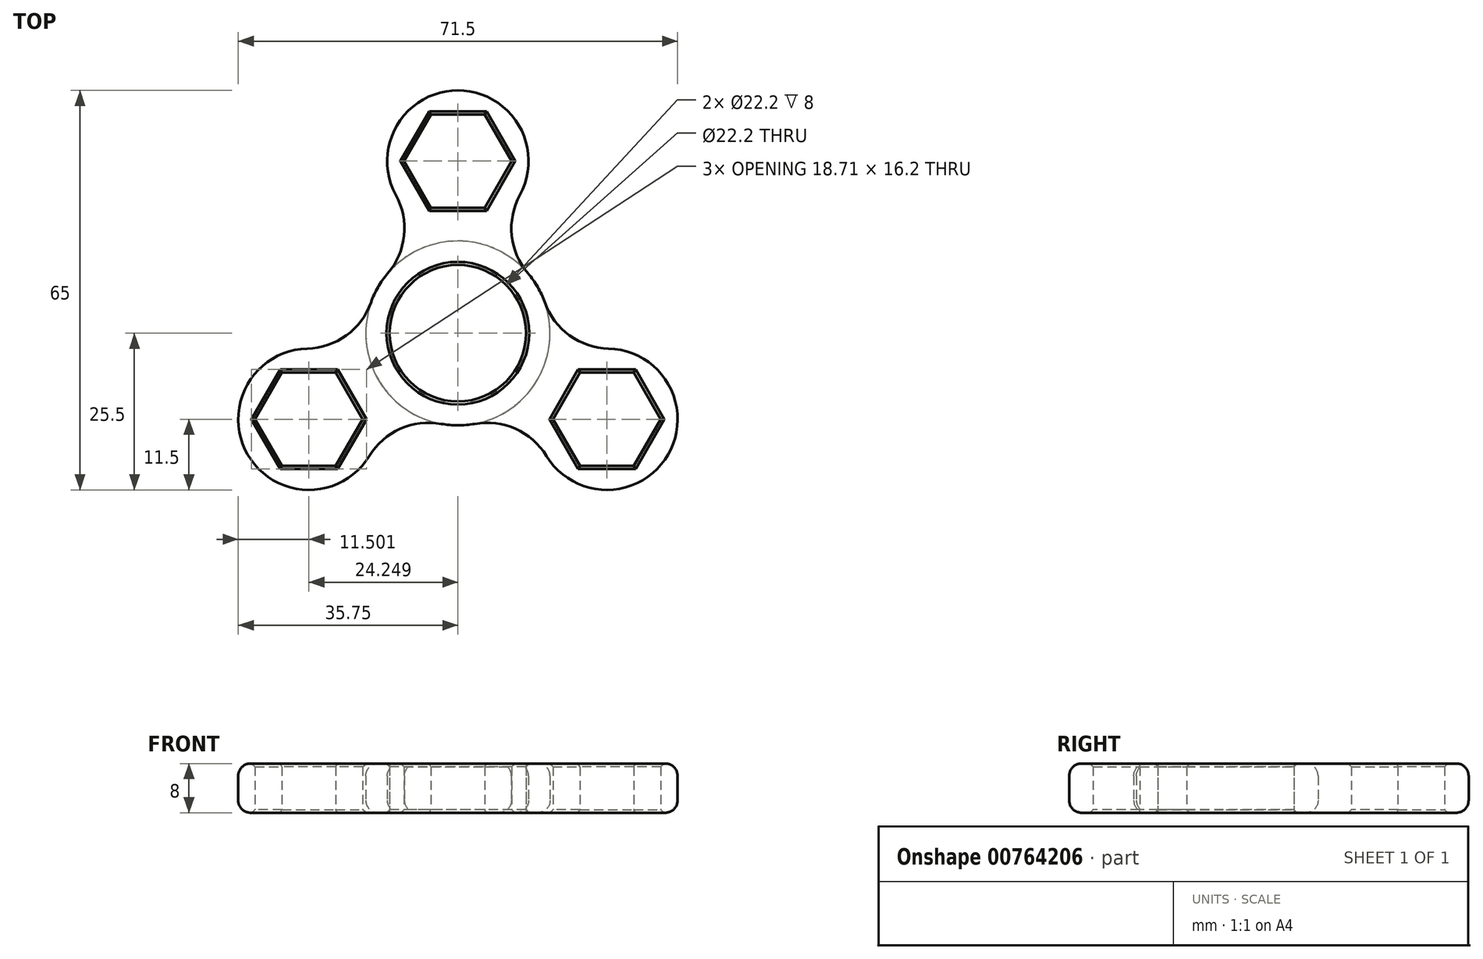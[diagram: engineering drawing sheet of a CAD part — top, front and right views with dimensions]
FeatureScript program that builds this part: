
annotation { "Feature Type Name" : "Feature", "Feature Type Description" : "" }
export const myFeature = defineFeature(function(context is Context, id is Id, definition is map)
    precondition{}
    {
        {
            var Q0;
            Q0=qCreatedBy(makeId("Top.planeOp"),FACE);
            var sketch = newSketch(context, id + "F0", { "sketchPlane" : qUnion([Q0])});
            skCircle(sketch, "E0", {"center": v(0, 0) * mm, "radius": 11.1 * mm});
            skArc(sketch, "E1", {"start": v(10.1, 22.48) * mm, "mid": v(0, 39.5) * mm, "end": v(-10.1, 22.48) * mm});
            skArc(sketch, "E2", {"start": v(-11.4, 9.74) * mm, "mid": v(0, -15) * mm, "end": v(11.4, 9.74) * mm});
            skArc(sketch, "E3", {"start": v(10.1, 22.48) * mm, "mid": v(8.77, 15.9) * mm, "end": v(11.4, 9.74) * mm});
            skLineSegment(sketch, "E4", {"start": v(0, -19.89) * mm, "end": v(0, 62.9) * mm, "construction": true});
            skArc(sketch, "E5.MirrorCS", {"start": v(-10.1, 22.48) * mm, "mid": v(-8.77, 15.9) * mm, "end": v(-11.4, 9.74) * mm});
            skCircle(sketch, "E6.cCircle", {"center": v(0, 28) * mm, "radius": 7.6 * mm, "construction": true});
            skLineSegment(sketch, "E6.0", {"start": v(4.39, 20.4) * mm, "end": v(-4.39, 20.4) * mm});
            skLineSegment(sketch, "E6.1", {"start": v(-4.39, 20.4) * mm, "end": v(-8.78, 28) * mm});
            skLineSegment(sketch, "E6.2", {"start": v(-8.78, 28) * mm, "end": v(-4.39, 35.6) * mm});
            skLineSegment(sketch, "E6.3", {"start": v(-4.39, 35.6) * mm, "end": v(4.39, 35.6) * mm});
            skLineSegment(sketch, "E6.4", {"start": v(4.39, 35.6) * mm, "end": v(8.78, 28) * mm});
            skLineSegment(sketch, "E6.5", {"start": v(8.78, 28) * mm, "end": v(4.39, 20.4) * mm});
            skPoint(sketch, "E6.0.midPoint", {"position": v(0, 20.4) * mm});
            skSolve(sketch);
        }
        {
            var Q0;
            Q0=makeQuery(id+"F0.imprint","IMPRINT",FACE,{"disambiguationData":[TD([[makeQuery(id+"F0.imprint","IMPRINT",EDGE,{"derivedFrom":sQuery(id+"F0.wireOp",EDGE,"E0")}),-1.0]])]});
            extrude(context, id + "F1", {"entities" : qUnion([Q0]), "depth" : 8 * mm, "offsetDistance" : 25 * mm});
        }
        {
            var Q0;
            Q0=makeQuery(id+"F1.opExtrude","SWEPT_BODY",BODY,{"disambiguationData":[OSD([sQuery(id+"F0.wireOp",EDGE,"E0"),sQuery(id+"F0.wireOp",EDGE,"PvTHQTtv-MwDr-1RPm-Ui1H-ZR7QVBU8jPbe"),sQuery(id+"F0.wireOp",EDGE,"E1"),sQuery(id+"F0.wireOp",EDGE,"E2"),sQuery(id+"F0.wireOp",EDGE,"E3"),sQuery(id+"F0.wireOp",EDGE,"E5.MirrorCS")])]});
            var Q1;
            Q1=makeQuery(id+"F1.opExtrude","CAP_EDGE",EDGE,{"disambiguationData":[OSD([sQuery(id+"F0.wireOp",EDGE,"E0")])],"isStart":false});
            circularPattern(context, id + "F2", {"entities" : qUnion([Q0]), "axis" : qUnion([Q1]), "angle" : 360 * degree, "instanceCount" : 3, "equalSpace" : true});
        }
        {
            var Q0;
            Q0=makeQuery(id+"F2.opPattern","COPY",EDGE,{"derivedFrom":makeQuery(id+"F1.opExtrude","CAP_EDGE",EDGE,{"disambiguationData":[OSD([sQuery(id+"F0.wireOp",EDGE,"E3")])],"isStart":false}),"instanceName":"2"});
            fillet(context, id + "F3", {"entities" : qUnion([Q0]), "radius" : 2 * mm, "tangentPropagation" : true, "allowEdgeOverflow" : false});
        }
        {
            var Q0;
            Q0=makeQuery(id+"F2.opPattern","COPY",EDGE,{"derivedFrom":makeQuery(id+"F1.opExtrude","CAP_EDGE",EDGE,{"disambiguationData":[OSD([sQuery(id+"F0.wireOp",EDGE,"E1")])],"isStart":false}),"instanceName":"1"});
            var Q1;
            Q1=makeQuery(id+"F1.opExtrude","CAP_EDGE",EDGE,{"disambiguationData":[OSD([sQuery(id+"F0.wireOp",EDGE,"E5.MirrorCS")])],"isStart":false});
            var Q2;
            Q2=makeQuery(id+"F2.opPattern","COPY",EDGE,{"derivedFrom":makeQuery(id+"F1.opExtrude","CAP_EDGE",EDGE,{"disambiguationData":[OSD([sQuery(id+"F0.wireOp",EDGE,"E1")])],"isStart":true}),"instanceName":"1"});
            var Q3;
            Q3=makeQuery(id+"F2.opPattern","COPY",EDGE,{"derivedFrom":makeQuery(id+"F1.opExtrude","CAP_EDGE",EDGE,{"disambiguationData":[OSD([sQuery(id+"F0.wireOp",EDGE,"E1")])],"isStart":true}),"instanceName":"2"});
            var Q4;
            Q4=makeQuery(id+"F1.opExtrude","CAP_EDGE",EDGE,{"disambiguationData":[OSD([sQuery(id+"F0.wireOp",EDGE,"E5.MirrorCS")])],"isStart":true});
            fillet(context, id + "F4", {"entities" : qUnion([Q0, Q1, Q2, Q3, Q4]), "radius" : 2 * mm, "tangentPropagation" : true, "allowEdgeOverflow" : false});
        }
        {
            var Q0;
            Q0=makeQuery(id+"F1.opExtrude","CAP_EDGE",EDGE,{"disambiguationData":[OSD([sQuery(id+"F0.wireOp",EDGE,"E6.0")])],"isStart":false});
            var Q1;
            Q1=makeQuery(id+"F1.opExtrude","CAP_EDGE",EDGE,{"disambiguationData":[OSD([sQuery(id+"F0.wireOp",EDGE,"E6.1")])],"isStart":false});
            var Q2;
            Q2=makeQuery(id+"F1.opExtrude","CAP_EDGE",EDGE,{"disambiguationData":[OSD([sQuery(id+"F0.wireOp",EDGE,"E6.5")])],"isStart":false});
            var Q3;
            Q3=makeQuery(id+"F1.opExtrude","CAP_EDGE",EDGE,{"disambiguationData":[OSD([sQuery(id+"F0.wireOp",EDGE,"E6.4")])],"isStart":false});
            var Q4;
            Q4=makeQuery(id+"F1.opExtrude","CAP_EDGE",EDGE,{"disambiguationData":[OSD([sQuery(id+"F0.wireOp",EDGE,"E6.3")])],"isStart":false});
            var Q5;
            Q5=makeQuery(id+"F1.opExtrude","CAP_EDGE",EDGE,{"disambiguationData":[OSD([sQuery(id+"F0.wireOp",EDGE,"E6.2")])],"isStart":false});
            var Q6;
            Q6=makeQuery(id+"F2.opPattern","COPY",EDGE,{"derivedFrom":makeQuery(id+"F1.opExtrude","CAP_EDGE",EDGE,{"disambiguationData":[OSD([sQuery(id+"F0.wireOp",EDGE,"E6.5")])],"isStart":false}),"instanceName":"1"});
            var Q7;
            Q7=makeQuery(id+"F2.opPattern","COPY",EDGE,{"derivedFrom":makeQuery(id+"F1.opExtrude","CAP_EDGE",EDGE,{"disambiguationData":[OSD([sQuery(id+"F0.wireOp",EDGE,"E6.0")])],"isStart":false}),"instanceName":"1"});
            var Q8;
            Q8=makeQuery(id+"F2.opPattern","COPY",EDGE,{"derivedFrom":makeQuery(id+"F1.opExtrude","CAP_EDGE",EDGE,{"disambiguationData":[OSD([sQuery(id+"F0.wireOp",EDGE,"E6.1")])],"isStart":false}),"instanceName":"1"});
            var Q9;
            Q9=makeQuery(id+"F2.opPattern","COPY",EDGE,{"derivedFrom":makeQuery(id+"F1.opExtrude","CAP_EDGE",EDGE,{"disambiguationData":[OSD([sQuery(id+"F0.wireOp",EDGE,"E6.2")])],"isStart":false}),"instanceName":"1"});
            var Q10;
            Q10=makeQuery(id+"F2.opPattern","COPY",EDGE,{"derivedFrom":makeQuery(id+"F1.opExtrude","CAP_EDGE",EDGE,{"disambiguationData":[OSD([sQuery(id+"F0.wireOp",EDGE,"E6.3")])],"isStart":false}),"instanceName":"1"});
            var Q11;
            Q11=makeQuery(id+"F2.opPattern","COPY",EDGE,{"derivedFrom":makeQuery(id+"F1.opExtrude","CAP_EDGE",EDGE,{"disambiguationData":[OSD([sQuery(id+"F0.wireOp",EDGE,"E6.4")])],"isStart":false}),"instanceName":"1"});
            var Q12;
            Q12=makeQuery(id+"F2.opPattern","COPY",EDGE,{"derivedFrom":makeQuery(id+"F1.opExtrude","CAP_EDGE",EDGE,{"disambiguationData":[OSD([sQuery(id+"F0.wireOp",EDGE,"E6.0")])],"isStart":false}),"instanceName":"2"});
            var Q13;
            Q13=makeQuery(id+"F2.opPattern","COPY",EDGE,{"derivedFrom":makeQuery(id+"F1.opExtrude","CAP_EDGE",EDGE,{"disambiguationData":[OSD([sQuery(id+"F0.wireOp",EDGE,"E6.1")])],"isStart":false}),"instanceName":"2"});
            var Q14;
            Q14=makeQuery(id+"F2.opPattern","COPY",EDGE,{"derivedFrom":makeQuery(id+"F1.opExtrude","CAP_EDGE",EDGE,{"disambiguationData":[OSD([sQuery(id+"F0.wireOp",EDGE,"E6.2")])],"isStart":false}),"instanceName":"2"});
            var Q15;
            Q15=makeQuery(id+"F2.opPattern","COPY",EDGE,{"derivedFrom":makeQuery(id+"F1.opExtrude","CAP_EDGE",EDGE,{"disambiguationData":[OSD([sQuery(id+"F0.wireOp",EDGE,"E6.3")])],"isStart":false}),"instanceName":"2"});
            var Q16;
            Q16=makeQuery(id+"F2.opPattern","COPY",EDGE,{"derivedFrom":makeQuery(id+"F1.opExtrude","CAP_EDGE",EDGE,{"disambiguationData":[OSD([sQuery(id+"F0.wireOp",EDGE,"E6.4")])],"isStart":false}),"instanceName":"2"});
            var Q17;
            Q17=makeQuery(id+"F2.opPattern","COPY",EDGE,{"derivedFrom":makeQuery(id+"F1.opExtrude","CAP_EDGE",EDGE,{"disambiguationData":[OSD([sQuery(id+"F0.wireOp",EDGE,"E6.5")])],"isStart":false}),"instanceName":"2"});
            var Q18;
            Q18=makeQuery(id+"F1.opExtrude","CAP_EDGE",EDGE,{"disambiguationData":[OSD([sQuery(id+"F0.wireOp",EDGE,"E0")])],"isStart":false});
            var Q19;
            Q19=makeQuery(id+"F1.opExtrude","CAP_EDGE",EDGE,{"disambiguationData":[OSD([sQuery(id+"F0.wireOp",EDGE,"E0")])],"isStart":true});
            var Q20;
            Q20=makeQuery(id+"F1.opExtrude","CAP_EDGE",EDGE,{"disambiguationData":[OSD([sQuery(id+"F0.wireOp",EDGE,"E6.1")])],"isStart":true});
            var Q21;
            Q21=makeQuery(id+"F1.opExtrude","CAP_EDGE",EDGE,{"disambiguationData":[OSD([sQuery(id+"F0.wireOp",EDGE,"E6.2")])],"isStart":true});
            var Q22;
            Q22=makeQuery(id+"F1.opExtrude","CAP_EDGE",EDGE,{"disambiguationData":[OSD([sQuery(id+"F0.wireOp",EDGE,"E6.3")])],"isStart":true});
            var Q23;
            Q23=makeQuery(id+"F1.opExtrude","CAP_EDGE",EDGE,{"disambiguationData":[OSD([sQuery(id+"F0.wireOp",EDGE,"E6.4")])],"isStart":true});
            var Q24;
            Q24=makeQuery(id+"F1.opExtrude","CAP_EDGE",EDGE,{"disambiguationData":[OSD([sQuery(id+"F0.wireOp",EDGE,"E6.5")])],"isStart":true});
            var Q25;
            Q25=makeQuery(id+"F1.opExtrude","CAP_EDGE",EDGE,{"disambiguationData":[OSD([sQuery(id+"F0.wireOp",EDGE,"E6.0")])],"isStart":true});
            var Q26;
            Q26=makeQuery(id+"F2.opPattern","COPY",EDGE,{"derivedFrom":makeQuery(id+"F1.opExtrude","CAP_EDGE",EDGE,{"disambiguationData":[OSD([sQuery(id+"F0.wireOp",EDGE,"E6.0")])],"isStart":true}),"instanceName":"1"});
            var Q27;
            Q27=makeQuery(id+"F2.opPattern","COPY",EDGE,{"derivedFrom":makeQuery(id+"F1.opExtrude","CAP_EDGE",EDGE,{"disambiguationData":[OSD([sQuery(id+"F0.wireOp",EDGE,"E6.5")])],"isStart":true}),"instanceName":"1"});
            var Q28;
            Q28=makeQuery(id+"F2.opPattern","COPY",EDGE,{"derivedFrom":makeQuery(id+"F1.opExtrude","CAP_EDGE",EDGE,{"disambiguationData":[OSD([sQuery(id+"F0.wireOp",EDGE,"E6.4")])],"isStart":true}),"instanceName":"1"});
            var Q29;
            Q29=makeQuery(id+"F2.opPattern","COPY",EDGE,{"derivedFrom":makeQuery(id+"F1.opExtrude","CAP_EDGE",EDGE,{"disambiguationData":[OSD([sQuery(id+"F0.wireOp",EDGE,"E6.3")])],"isStart":true}),"instanceName":"1"});
            var Q30;
            Q30=makeQuery(id+"F2.opPattern","COPY",EDGE,{"derivedFrom":makeQuery(id+"F1.opExtrude","CAP_EDGE",EDGE,{"disambiguationData":[OSD([sQuery(id+"F0.wireOp",EDGE,"E6.2")])],"isStart":true}),"instanceName":"1"});
            var Q31;
            Q31=makeQuery(id+"F2.opPattern","COPY",EDGE,{"derivedFrom":makeQuery(id+"F1.opExtrude","CAP_EDGE",EDGE,{"disambiguationData":[OSD([sQuery(id+"F0.wireOp",EDGE,"E6.1")])],"isStart":true}),"instanceName":"1"});
            var Q32;
            Q32=makeQuery(id+"F2.opPattern","COPY",EDGE,{"derivedFrom":makeQuery(id+"F1.opExtrude","CAP_EDGE",EDGE,{"disambiguationData":[OSD([sQuery(id+"F0.wireOp",EDGE,"E6.5")])],"isStart":true}),"instanceName":"2"});
            var Q33;
            Q33=makeQuery(id+"F2.opPattern","COPY",EDGE,{"derivedFrom":makeQuery(id+"F1.opExtrude","CAP_EDGE",EDGE,{"disambiguationData":[OSD([sQuery(id+"F0.wireOp",EDGE,"E6.0")])],"isStart":true}),"instanceName":"2"});
            var Q34;
            Q34=makeQuery(id+"F2.opPattern","COPY",EDGE,{"derivedFrom":makeQuery(id+"F1.opExtrude","CAP_EDGE",EDGE,{"disambiguationData":[OSD([sQuery(id+"F0.wireOp",EDGE,"E6.1")])],"isStart":true}),"instanceName":"2"});
            var Q35;
            Q35=makeQuery(id+"F2.opPattern","COPY",EDGE,{"derivedFrom":makeQuery(id+"F1.opExtrude","CAP_EDGE",EDGE,{"disambiguationData":[OSD([sQuery(id+"F0.wireOp",EDGE,"E6.2")])],"isStart":true}),"instanceName":"2"});
            var Q36;
            Q36=makeQuery(id+"F2.opPattern","COPY",EDGE,{"derivedFrom":makeQuery(id+"F1.opExtrude","CAP_EDGE",EDGE,{"disambiguationData":[OSD([sQuery(id+"F0.wireOp",EDGE,"E6.3")])],"isStart":true}),"instanceName":"2"});
            var Q37;
            Q37=makeQuery(id+"F2.opPattern","COPY",EDGE,{"derivedFrom":makeQuery(id+"F1.opExtrude","CAP_EDGE",EDGE,{"disambiguationData":[OSD([sQuery(id+"F0.wireOp",EDGE,"E6.4")])],"isStart":true}),"instanceName":"2"});
            chamfer(context, id + "F5", {"entities" : qUnion([Q0, Q1, Q2, Q3, Q4, Q5, Q6, Q7, Q8, Q9, Q10, Q11, Q12, Q13, Q14, Q15, Q16, Q17, Q18, Q19, Q20, Q21, Q22, Q23, Q24, Q25, Q26, Q27, Q28, Q29, Q30, Q31, Q32, Q33, Q34, Q35, Q36, Q37]), "width" : 0.5 * mm, "tangentPropagation" : true});
        }
    });
